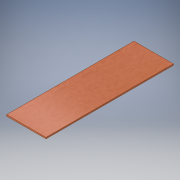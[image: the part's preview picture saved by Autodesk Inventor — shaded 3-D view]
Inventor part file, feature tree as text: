
AUTODESK INVENTOR PART (.ipt)
format: ipt  version: 2018 (Build 220112000, 112)  size: 103,424 bytes
history: native  units: mm
features: extrude x1
ambient origin geometry x8: Origin, YZ Plane, XZ Plane, XY Plane, X Axis, Y Axis, Z Axis, Center Point
bodies: Volumenkörper1 (feature_tree)
feature tree (1):
  extrude  "Extrusion1"  Depth=34.0mm
